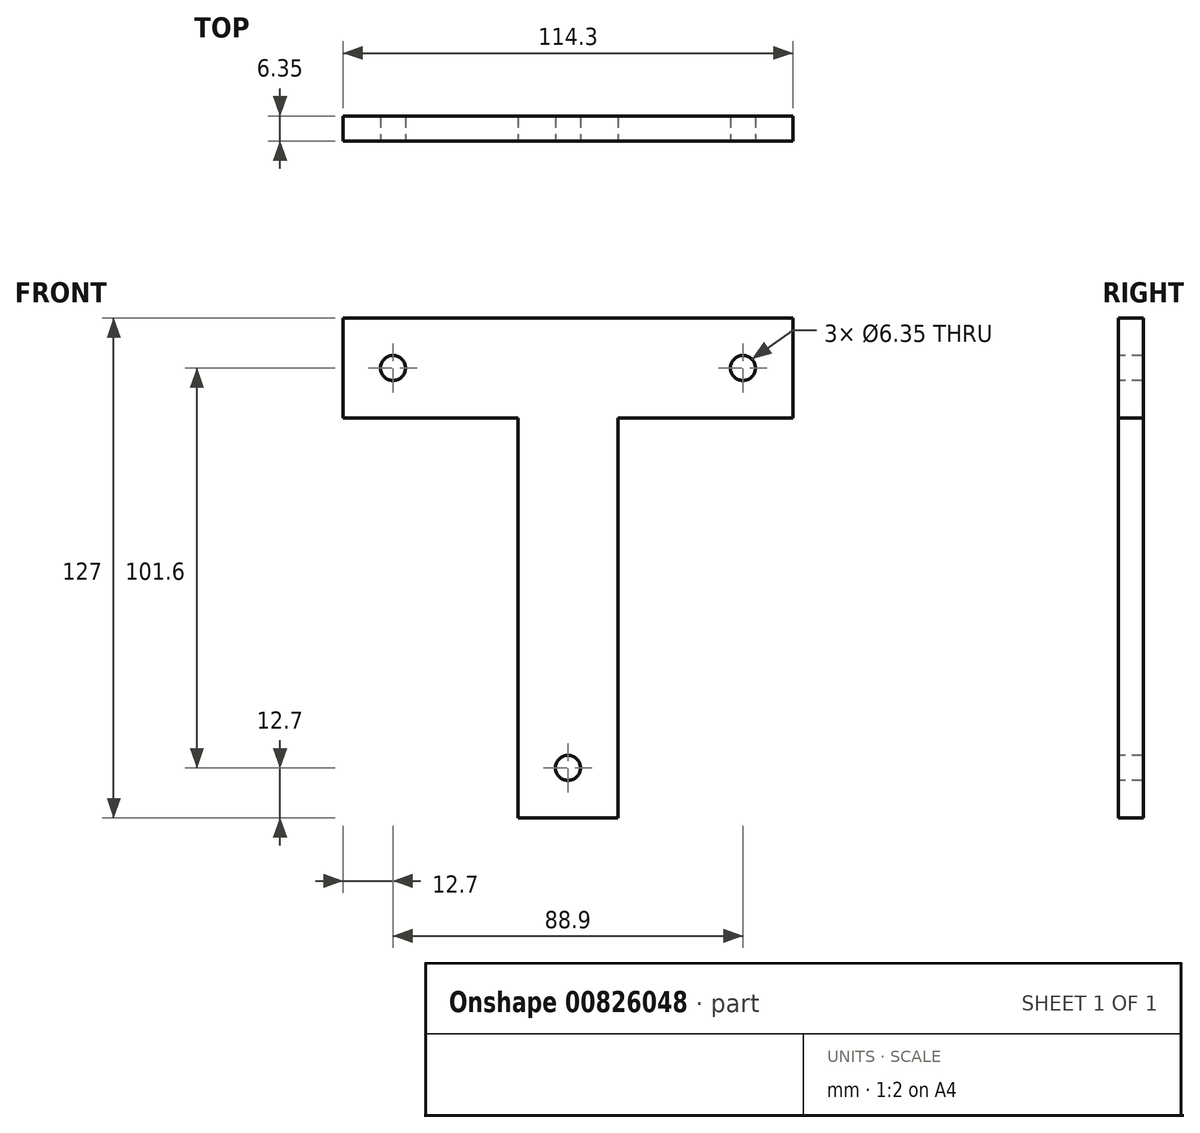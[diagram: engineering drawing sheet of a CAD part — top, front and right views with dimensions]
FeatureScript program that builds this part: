
annotation { "Feature Type Name" : "Feature", "Feature Type Description" : "" }
export const myFeature = defineFeature(function(context is Context, id is Id, definition is map)
    precondition{}
    {
        {
            var Q0;
            Q0=qCreatedBy(makeId("Front.planeOp"),FACE);
            var sketch = newSketch(context, id + "F0", { "sketchPlane" : qUnion([Q0])});
            skLineSegment(sketch, "E0.bottom", {"start": v(12.7, -63.5) * mm, "end": v(-12.7, -63.5) * mm});
            skLineSegment(sketch, "E0.top", {"start": v(57.15, 63.5) * mm, "end": v(-57.15, 63.5) * mm});
            skLineSegment(sketch, "E0.left", {"start": v(57.15, 38.1) * mm, "end": v(57.15, 63.5) * mm});
            skLineSegment(sketch, "E0.right", {"start": v(-57.15, 38.1) * mm, "end": v(-57.15, 63.5) * mm});
            skPoint(sketch, "E0.middle", {"position": v(0, 0) * mm});
            skLineSegment(sketch, "E1", {"start": v(-57.15, 38.1) * mm, "end": v(-12.7, 38.1) * mm});
            skLineSegment(sketch, "E2", {"start": v(0, 0) * mm, "end": v(0, -63.5) * mm, "construction": true});
            skLineSegment(sketch, "E3.0", {"start": v(-12.7, 38.1) * mm, "end": v(-12.7, -63.5) * mm});
            skLineSegment(sketch, "E4.0", {"start": v(12.7, 38.1) * mm, "end": v(12.7, -63.5) * mm});
            skPoint(sketch, "E5.orphan", {"position": v(0, 63.5) * mm});
            skLineSegment(sketch, "E6.trimOffspring", {"start": v(12.7, 38.1) * mm, "end": v(57.15, 38.1) * mm});
            skPoint(sketch, "E7.orphan", {"position": v(-57.15, -63.5) * mm});
            skPoint(sketch, "E8.orphan", {"position": v(57.15, -63.5) * mm});
            skPoint(sketch, "E9", {"position": v(-44.45, 50.8) * mm});
            skPoint(sketch, "E10", {"position": v(44.45, 50.8) * mm});
            skPoint(sketch, "E11", {"position": v(0, -50.8) * mm});
            skSolve(sketch);
        }
        {
            var Q0;
            Q0=makeQuery(id+"F0.imprint","IMPRINT",FACE,{"disambiguationData":[TD([[makeQuery(id+"F0.imprint","IMPRINT",EDGE,{"derivedFrom":sQuery(id+"F0.wireOp",EDGE,"E0.bottom")}),-1.0]])]});
            extrude(context, id + "F1", {"entities" : qUnion([Q0]), "oppositeDirection" : true, "depth" : 6.35 * mm, "offsetDistance" : 25.4 * mm});
        }
        {
            var Q0;
            Q0=sQuery(id+"F0.wireOp",VERTEX,"E9");
            var Q1;
            Q1=sQuery(id+"F0.wireOp",VERTEX,"E10");
            var Q2;
            Q2=sQuery(id+"F0.wireOp",VERTEX,"E11");
            var Q3;
            Q3=makeQuery(id+"F1.opExtrude","SWEPT_BODY",BODY,{"disambiguationData":[OSD([sQuery(id+"F0.wireOp",EDGE,"E0.bottom"),sQuery(id+"F0.wireOp",EDGE,"E0.top"),sQuery(id+"F0.wireOp",EDGE,"E0.left"),sQuery(id+"F0.wireOp",EDGE,"E0.right"),sQuery(id+"F0.wireOp",EDGE,"E1"),sQuery(id+"F0.wireOp",EDGE,"E3.0"),sQuery(id+"F0.wireOp",EDGE,"E4.0"),sQuery(id+"F0.wireOp",EDGE,"E6.trimOffspring")])]});
            hole(context, id + "F2", {"style" : HoleStyle.SIMPLE, "endStyle" : HoleEndStyle.THROUGH, "holeDiameter" : 6.35 * mm, "majorDiameter" : 6.35 * mm, "isTappedThrough" : true, "tappedDepth" : 12.7 * mm, "tapClearance" : 3, "locations" : qUnion([Q0, Q1, Q2]), "scope" : qUnion([Q3])});
        }
    });
